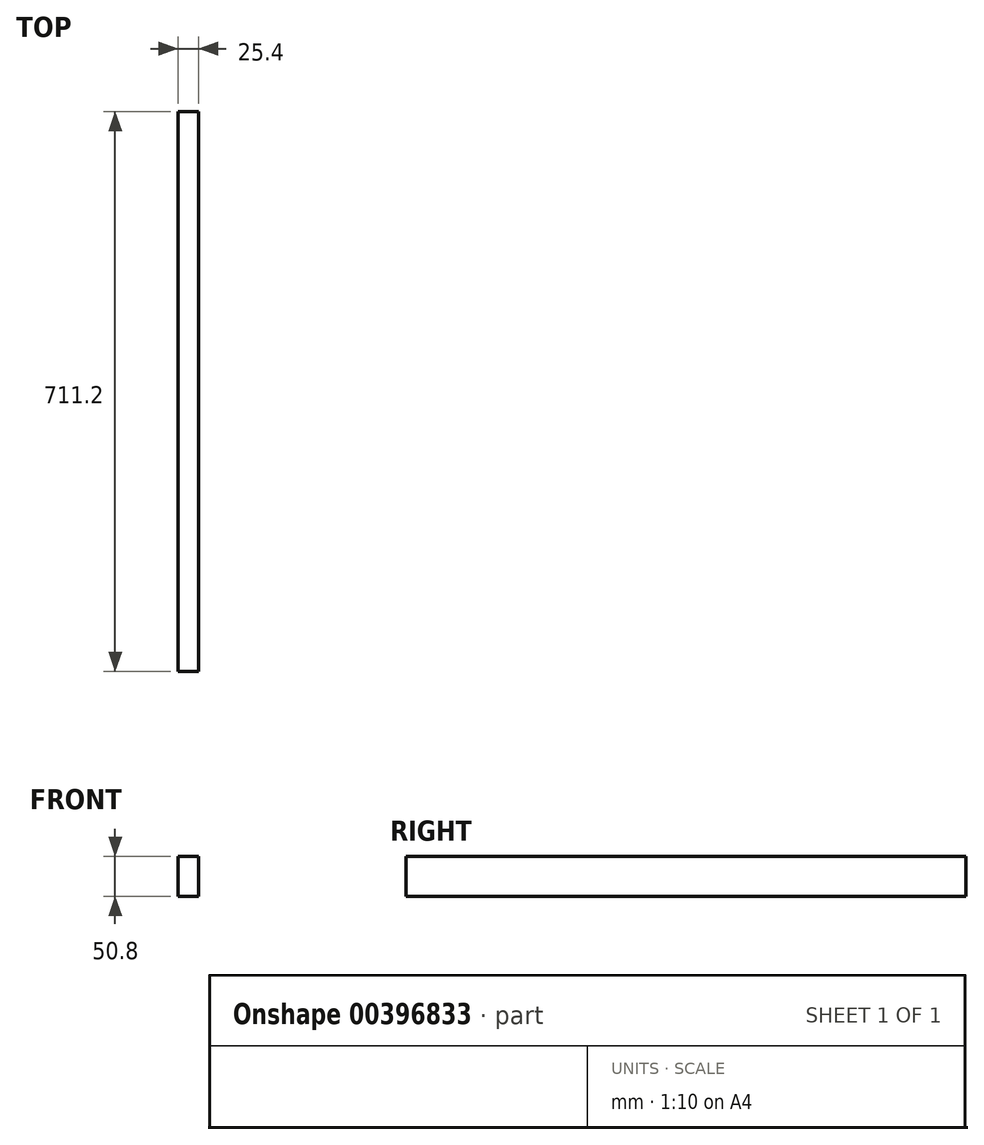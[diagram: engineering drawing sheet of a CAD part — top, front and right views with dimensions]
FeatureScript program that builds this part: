
annotation { "Feature Type Name" : "Feature", "Feature Type Description" : "" }
export const myFeature = defineFeature(function(context is Context, id is Id, definition is map)
    precondition{}
    {
        {
            var Q0;
            Q0=qCreatedBy(makeId("Right.planeOp"),FACE);
            var sketch = newSketch(context, id + "F0", { "sketchPlane" : qUnion([Q0])});
            skLineSegment(sketch, "E0.bottom", {"start": v(-355.6, 25.4) * mm, "end": v(355.6, 25.4) * mm});
            skLineSegment(sketch, "E0.top", {"start": v(-355.6, -25.4) * mm, "end": v(355.6, -25.4) * mm});
            skLineSegment(sketch, "E0.left", {"start": v(-355.6, 25.4) * mm, "end": v(-355.6, -25.4) * mm});
            skLineSegment(sketch, "E0.right", {"start": v(355.6, 25.4) * mm, "end": v(355.6, -25.4) * mm});
            skPoint(sketch, "E0.middle", {"position": v(0, 0) * mm});
            skSolve(sketch);
        }
        {
            var Q0;
            Q0=makeQuery(id+"F0.imprint","IMPRINT",FACE,{"disambiguationData":[TD([[makeQuery(id+"F0.imprint","IMPRINT",EDGE,{"derivedFrom":sQuery(id+"F0.wireOp",EDGE,"E0.bottom")}),-1.0]])]});
            extrude(context, id + "F1", {"entities" : qUnion([Q0]), "depth" : 25.4 * mm});
        }
    });
